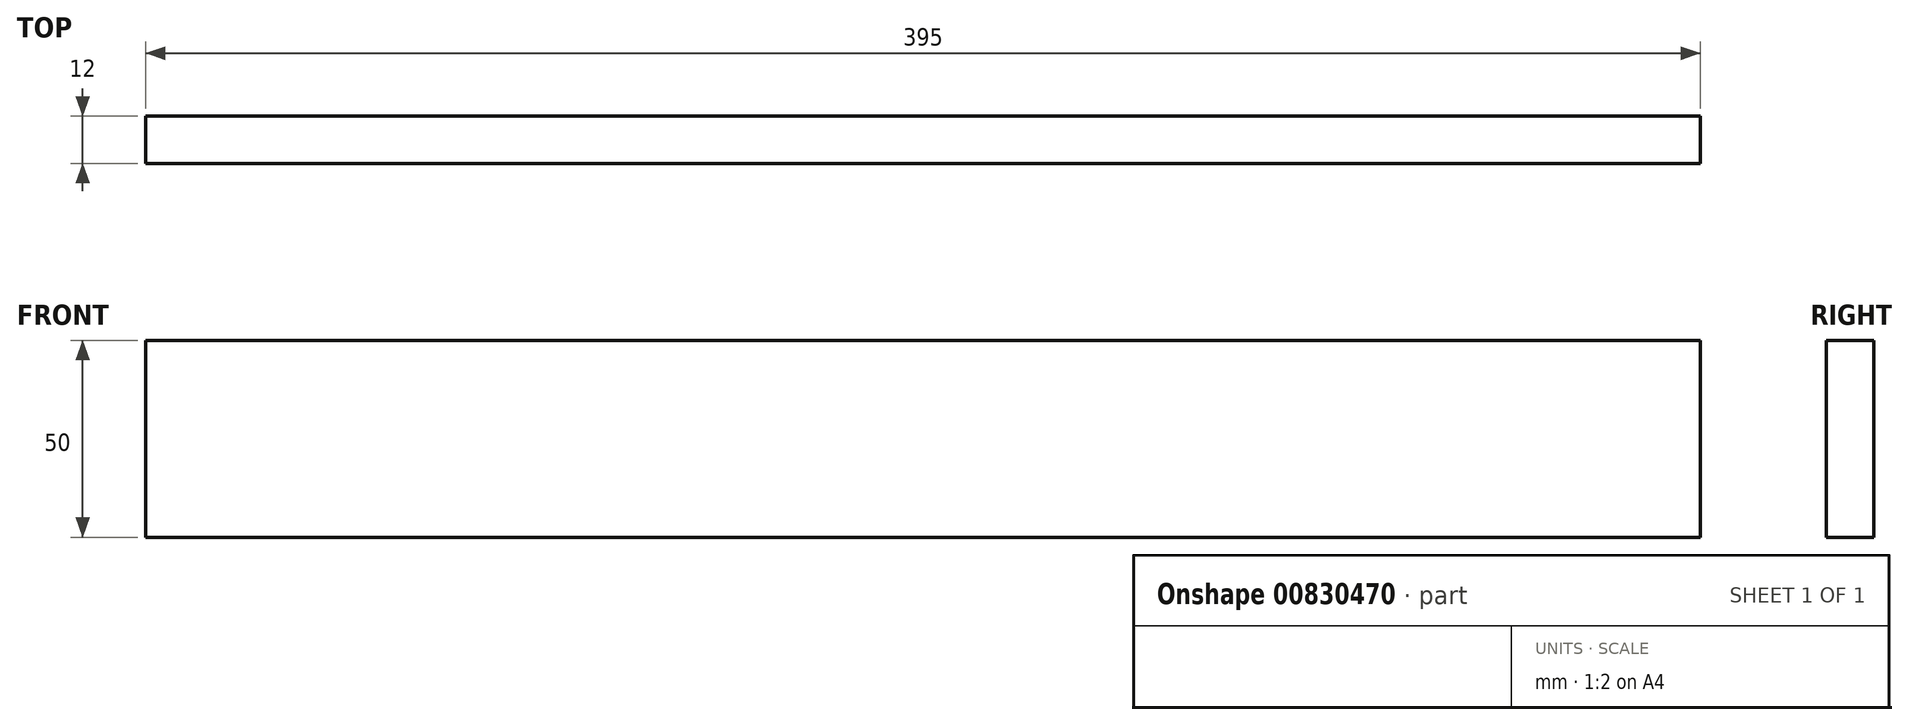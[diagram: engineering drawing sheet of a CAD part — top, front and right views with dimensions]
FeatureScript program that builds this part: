
annotation { "Feature Type Name" : "Feature", "Feature Type Description" : "" }
export const myFeature = defineFeature(function(context is Context, id is Id, definition is map)
    precondition{}
    {
        {
            var Q0;
            Q0=qCreatedBy(makeId("Front.planeOp"),FACE);
            var sketch = newSketch(context, id + "F0", { "sketchPlane" : qUnion([Q0])});
            skLineSegment(sketch, "E0.bottom", {"start": v(197.5, 25) * mm, "end": v(-197.5, 25) * mm});
            skLineSegment(sketch, "E0.top", {"start": v(197.5, -25) * mm, "end": v(-197.5, -25) * mm});
            skLineSegment(sketch, "E0.left", {"start": v(197.5, 25) * mm, "end": v(197.5, -25) * mm});
            skLineSegment(sketch, "E0.right", {"start": v(-197.5, 25) * mm, "end": v(-197.5, -25) * mm});
            skPoint(sketch, "E0.middle", {"position": v(0, 0) * mm});
            skSolve(sketch);
        }
        {
            var Q0;
            Q0=qSketchRegion(id+"F0",true);
            extrude(context, id + "F1", {"entities" : qUnion([Q0]), "depth" : 12 * mm, "offsetDistance" : 25 * mm});
        }
    });
